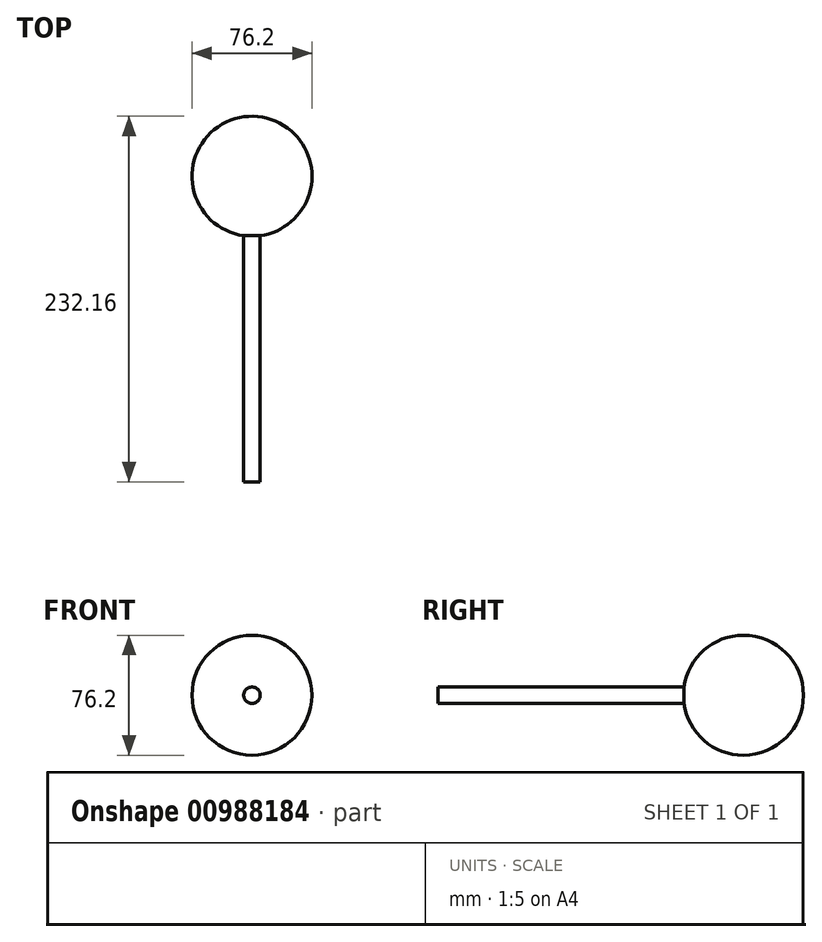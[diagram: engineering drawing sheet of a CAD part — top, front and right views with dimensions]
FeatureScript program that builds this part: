
annotation { "Feature Type Name" : "Feature", "Feature Type Description" : "" }
export const myFeature = defineFeature(function(context is Context, id is Id, definition is map)
    precondition{}
    {
        {
            var Q0;
            Q0=qCreatedBy(makeId("Front.planeOp"),FACE);
            var sketch = newSketch(context, id + "F0", { "sketchPlane" : qUnion([Q0])});
            skArc(sketch, "E0", {"start": v(0, 38.1) * mm, "mid": v(-38.1, 0) * mm, "end": v(0, -38.1) * mm});
            skLineSegment(sketch, "E1", {"start": v(0, 81.1) * mm, "end": v(0, -79.46) * mm, "construction": true});
            skLineSegment(sketch, "E2", {"start": v(0, 38.1) * mm, "end": v(0, -38.1) * mm});
            skSolve(sketch);
        }
        {
            var Q0;
            Q0=makeQuery(id+"F0.imprint","IMPRINT",FACE,{"disambiguationData":[TD([[makeQuery(id+"F0.imprint","IMPRINT",EDGE,{"derivedFrom":sQuery(id+"F0.wireOp",EDGE,"E0")}),1.0]])]});
            var Q1;
            Q1=sQuery(id+"F0.wireOp",EDGE,"E2");
            revolve(context, id + "F1", {"surfaceOperationType" : NewSurfaceOperationType.NEW, "entities" : qUnion([Q0]), "axis" : qUnion([Q1]), "revolveType" : RevolveType.FULL});
        }
        {
            var Q0;
            Q0=qCreatedBy(makeId("Front.planeOp"),FACE);
            var sketch = newSketch(context, id + "F2", { "sketchPlane" : qUnion([Q0])});
            skCircle(sketch, "E3", {"center": v(0, 0) * mm, "radius": 5.23 * mm});
            skSolve(sketch);
        }
        {
            var Q0;
            Q0=makeQuery(id+"F2.imprint","IMPRINT",FACE,{"disambiguationData":[TD([[makeQuery(id+"F2.imprint","IMPRINT",EDGE,{"derivedFrom":sQuery(id+"F2.wireOp",EDGE,"E3")}),1.0]])]});
            extrude(context, id + "F3", {"entities" : qUnion([Q0]), "operationType" : NewBodyOperationType.ADD, "depth" : 194.06 * mm, "offsetDistance" : 25.4 * mm});
        }
    });
